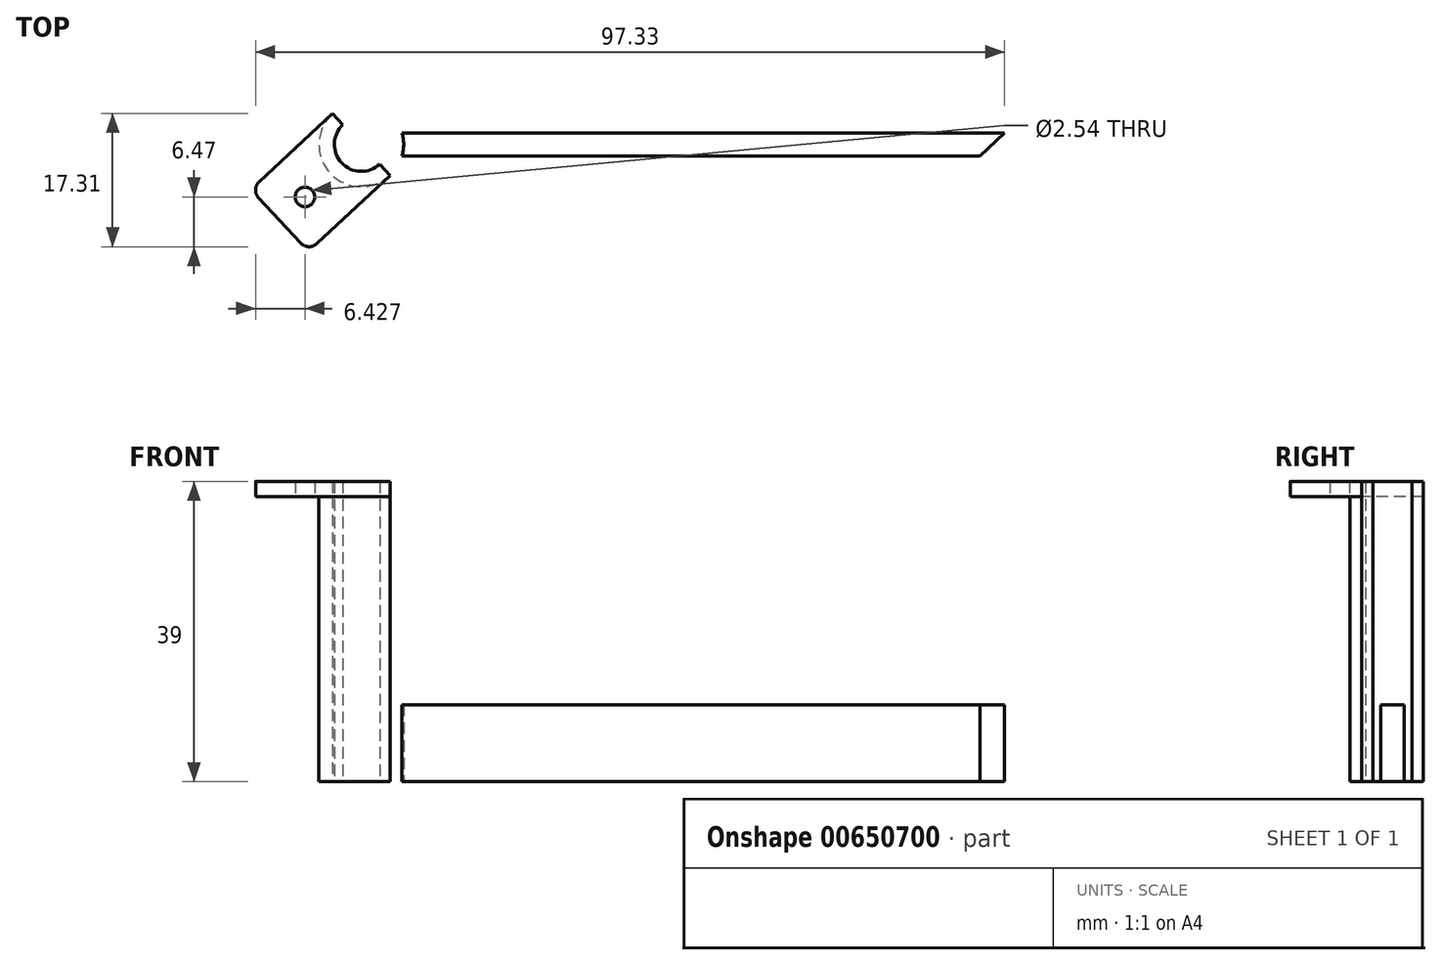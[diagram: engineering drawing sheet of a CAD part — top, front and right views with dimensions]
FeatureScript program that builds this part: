
annotation { "Feature Type Name" : "Feature", "Feature Type Description" : "" }
export const myFeature = defineFeature(function(context is Context, id is Id, definition is map)
    precondition{}
    {
        {
            var Q0;
            Q0=qCreatedBy(makeId("Top.planeOp"),FACE);
            var sketch = newSketch(context, id + "F0", { "sketchPlane" : qUnion([Q0])});
            skCircle(sketch, "E0", {"center": v(-44.5, 0) * mm, "radius": 3.5 * mm});
            skCircle(sketch, "E1", {"center": v(-44.5, 0) * mm, "radius": 5.5 * mm});
            skLineSegment(sketch, "E2", {"start": v(-39.2, 1.5) * mm, "end": v(39.1, 1.5) * mm});
            skLineSegment(sketch, "E3.MirrorCS", {"start": v(-39.2, -1.5) * mm, "end": v(35.87, -1.5) * mm});
            skLineSegment(sketch, "E4", {"start": v(39.1, 1.5) * mm, "end": v(35.87, -1.5) * mm});
            skPoint(sketch, "E5.orphan", {"position": v(39.1, -1.5) * mm});
            skLineSegment(sketch, "E6.bottom", {"start": v(-48.25, 4.02) * mm, "end": v(-40.75, -4.02) * mm});
            skLineSegment(sketch, "E6.top", {"start": v(-57.83, -6.96) * mm, "end": v(-52.38, -12.81) * mm});
            skLineSegment(sketch, "E6.left", {"start": v(-48.25, 4.02) * mm, "end": v(-57.76, -4.84) * mm});
            skLineSegment(sketch, "E6.right", {"start": v(-40.75, -4.02) * mm, "end": v(-50.26, -12.89) * mm});
            skPoint(sketch, "E7", {"position": v(-40.75, -4.02) * mm});
            skCircle(sketch, "E8", {"center": v(-51.81, -6.82) * mm, "radius": 1.27 * mm});
            skPoint(sketch, "E9.visualSharp", {"position": v(-51.35, -13.91) * mm});
            skArc(sketch, "E9.filletArc", {"start": v(-52.38, -12.81) * mm, "mid": v(-51.33, -13.3) * mm, "end": v(-50.26, -12.89) * mm});
            skPoint(sketch, "E10.visualSharp", {"position": v(-58.86, -5.87) * mm});
            skArc(sketch, "E10.filletArc", {"start": v(-57.76, -4.84) * mm, "mid": v(-58.23, -5.89) * mm, "end": v(-57.83, -6.96) * mm});
            skSolve(sketch);
        }
        {
            var Q0;
            {var subQ0=sQuery(id+"F0.wireOp",EDGE,"E2");Q0=makeQuery(id+"F0.imprint","IMPRINT",FACE,{"disambiguationData":[TD([[makeQuery(id+"F0.imprint","IMPRINT",EDGE,{"derivedFrom":subQ0}),-1.0]])]});}
            extrude(context, id + "F1", {"entities" : qUnion([Q0]), "depth" : 10 * mm});
        }
        {
            var Q0;
            Q0=makeQuery(id+"F0.imprint","IMPRINT",FACE,{"disambiguationData":[TD([[makeQuery(id+"F0.imprint","IMPRINT",EDGE,{"derivedFrom":sQuery(id+"F0.wireOp",EDGE,"E0")}),-1.0]])]});
            var Q1;
            Q1=makeQuery(id+"F0.imprint","IMPRINT",FACE,{"disambiguationData":[TD([[makeQuery(id+"F0.imprint","IMPRINT",EDGE,{"derivedFrom":sQuery(id+"F0.wireOp",EDGE,"d6ee0b0e-3c25-4719-a539-6223edddca480.MirrorC")}),1.0]])]});
            var Q2;
            {var subQ3=sQuery(id+"F0.wireOp",EDGE,"E6.bottom");var subQ6=sQuery(id+"F0.wireOp",EDGE,"E0");var subQ7=makeQuery(id+"F0.imprint","INTERSECT",VERTEX,{"disambiguationData":[OD(0.0)],"derivedFrom":[subQ6,subQ3]});Q2=makeQuery(id+"F0.imprint","IMPRINT",FACE,{"disambiguationData":[TD([[makeQuery(id+"F0.imprint","IMPRINT",EDGE,{"disambiguationData":[TD([[subQ7,1.0]])],"derivedFrom":subQ6}),-1.0]])]});}
            extrude(context, id + "F2", {"entities" : qUnion([Q0, Q1, Q2]), "operationType" : NewBodyOperationType.ADD, "depth" : 39 * mm, "offsetDistance" : 25 * mm});
        }
        {
            var Q0;
            Q0=makeQuery(id+"F0.imprint","IMPRINT",FACE,{"disambiguationData":[TD([[makeQuery(id+"F0.imprint","IMPRINT",EDGE,{"derivedFrom":sQuery(id+"F0.wireOp",EDGE,"E6.top")}),1.0]])]});
            var sketch = newSketch(context, id + "F3", { "sketchPlane" : qUnion([Q0])});
            skSolve(sketch);
        }
        {
            var Q0;
            Q0=makeQuery(id+"F3.imprint","IMPRINT",FACE,{"disambiguationData":[TD([[makeQuery(id+"F3.imprint","IMPRINT",EDGE,{"derivedFrom":makeQuery(id+"F0.imprint","IMPRINT",EDGE,{"derivedFrom":sQuery(id+"F0.wireOp",EDGE,"E6.top")})}),1.0]])]});
            extrude(context, id + "F4", {"entities" : qUnion([Q0]), "operationType" : NewBodyOperationType.ADD, "depth" : 39 * mm, "offsetDistance" : 25 * mm});
        }
        {
            var Q0;
            Q0=makeQuery(id+"F0.imprint","IMPRINT",FACE,{"disambiguationData":[TD([[makeQuery(id+"F0.imprint","IMPRINT",EDGE,{"derivedFrom":sQuery(id+"F0.wireOp",EDGE,"E6.top")}),1.0]])]});
            extrude(context, id + "F5", {"entities" : qUnion([Q0]), "operationType" : NewBodyOperationType.REMOVE, "depth" : 37 * mm, "offsetDistance" : 25 * mm});
        }
    });
